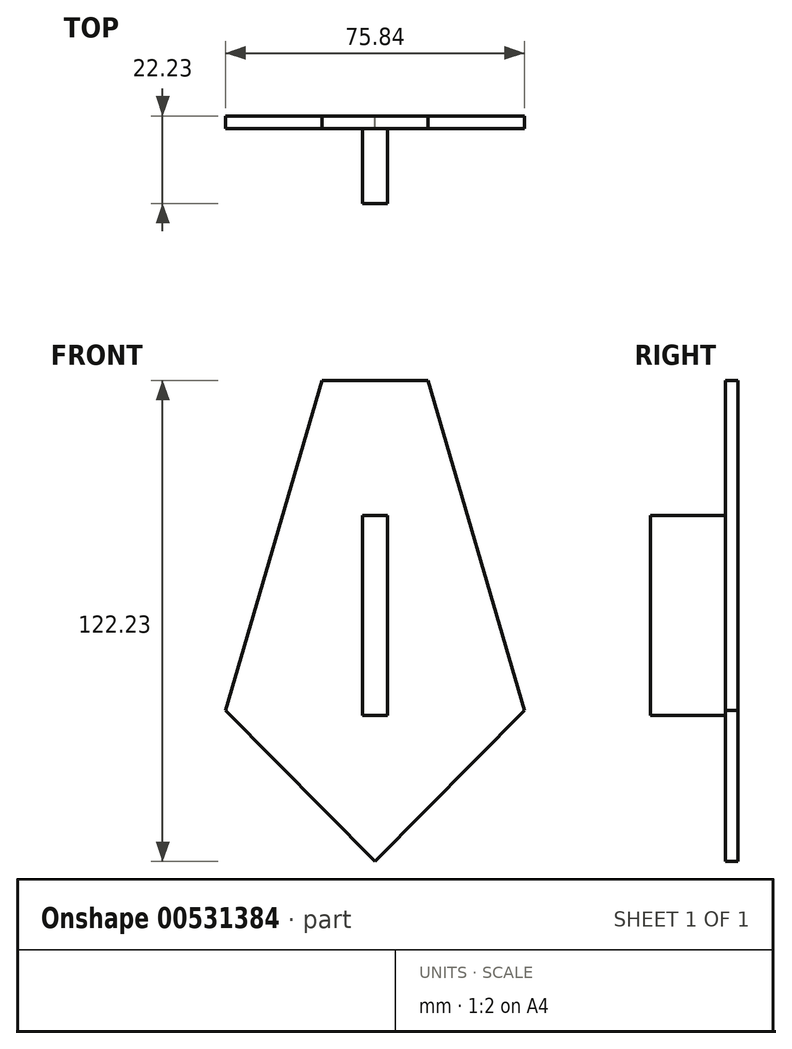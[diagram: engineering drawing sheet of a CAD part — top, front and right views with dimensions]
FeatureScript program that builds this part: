
annotation { "Feature Type Name" : "Feature", "Feature Type Description" : "" }
export const myFeature = defineFeature(function(context is Context, id is Id, definition is map)
    precondition{}
    {
        {
            var Q0;
            Q0=qCreatedBy(makeId("Front.planeOp"),FACE);
            var sketch = newSketch(context, id + "F0", { "sketchPlane" : qUnion([Q0])});
            skLineSegment(sketch, "E0", {"start": v(13.5, 83.5) * mm, "end": v(37.92, -0.32) * mm});
            skLineSegment(sketch, "E1", {"start": v(-13.5, 83.5) * mm, "end": v(-37.92, -0.32) * mm});
            skLineSegment(sketch, "E2", {"start": v(-37.92, -0.32) * mm, "end": v(0, -38.73) * mm});
            skLineSegment(sketch, "E3", {"start": v(0, -38.73) * mm, "end": v(37.92, -0.32) * mm});
            skLineSegment(sketch, "E4", {"start": v(-13.5, 83.5) * mm, "end": v(13.5, 83.5) * mm});
            skPoint(sketch, "E5", {"position": v(0, 83.5) * mm});
            skSolve(sketch);
        }
        {
            var Q0;
            Q0=makeQuery(id+"F0.imprint","IMPRINT",FACE,{"disambiguationData":[TD([[makeQuery(id+"F0.imprint","IMPRINT",EDGE,{"derivedFrom":sQuery(id+"F0.wireOp",EDGE,"E0")}),-1.0]])]});
            extrude(context, id + "F1", {"entities" : qUnion([Q0]), "depth" : 3.17 * mm, "offsetDistance" : 25.4 * mm});
        }
        {
            var Q0;
            Q0=makeQuery(id+"F1.opExtrude","CAP_FACE",FACE,{"disambiguationData":[OSD([sQuery(id+"F0.wireOp",EDGE,"E0"),sQuery(id+"F0.wireOp",EDGE,"E1"),sQuery(id+"F0.wireOp",EDGE,"E2"),sQuery(id+"F0.wireOp",EDGE,"E3"),sQuery(id+"F0.wireOp",EDGE,"E4")])],"isStart":false});
            var sketch = newSketch(context, id + "F2", { "sketchPlane" : qUnion([Q0])});
            skLineSegment(sketch, "E6.bottom", {"start": v(3.18, -1.6) * mm, "end": v(-3.17, -1.6) * mm});
            skLineSegment(sketch, "E6.top", {"start": v(3.18, 49.2) * mm, "end": v(-3.17, 49.2) * mm});
            skLineSegment(sketch, "E6.left", {"start": v(3.17, -1.6) * mm, "end": v(3.17, 49.2) * mm});
            skLineSegment(sketch, "E6.right", {"start": v(-3.18, -1.6) * mm, "end": v(-3.18, 49.2) * mm});
            skPoint(sketch, "E6.middle", {"position": v(0, 23.8) * mm});
            skSolve(sketch);
        }
        {
            var Q0;
            Q0=qSketchRegion(id+"F2",true);
            extrude(context, id + "F3", {"entities" : qUnion([Q0]), "operationType" : NewBodyOperationType.ADD, "depth" : 19.05 * mm, "offsetDistance" : 25.4 * mm});
        }
    });
